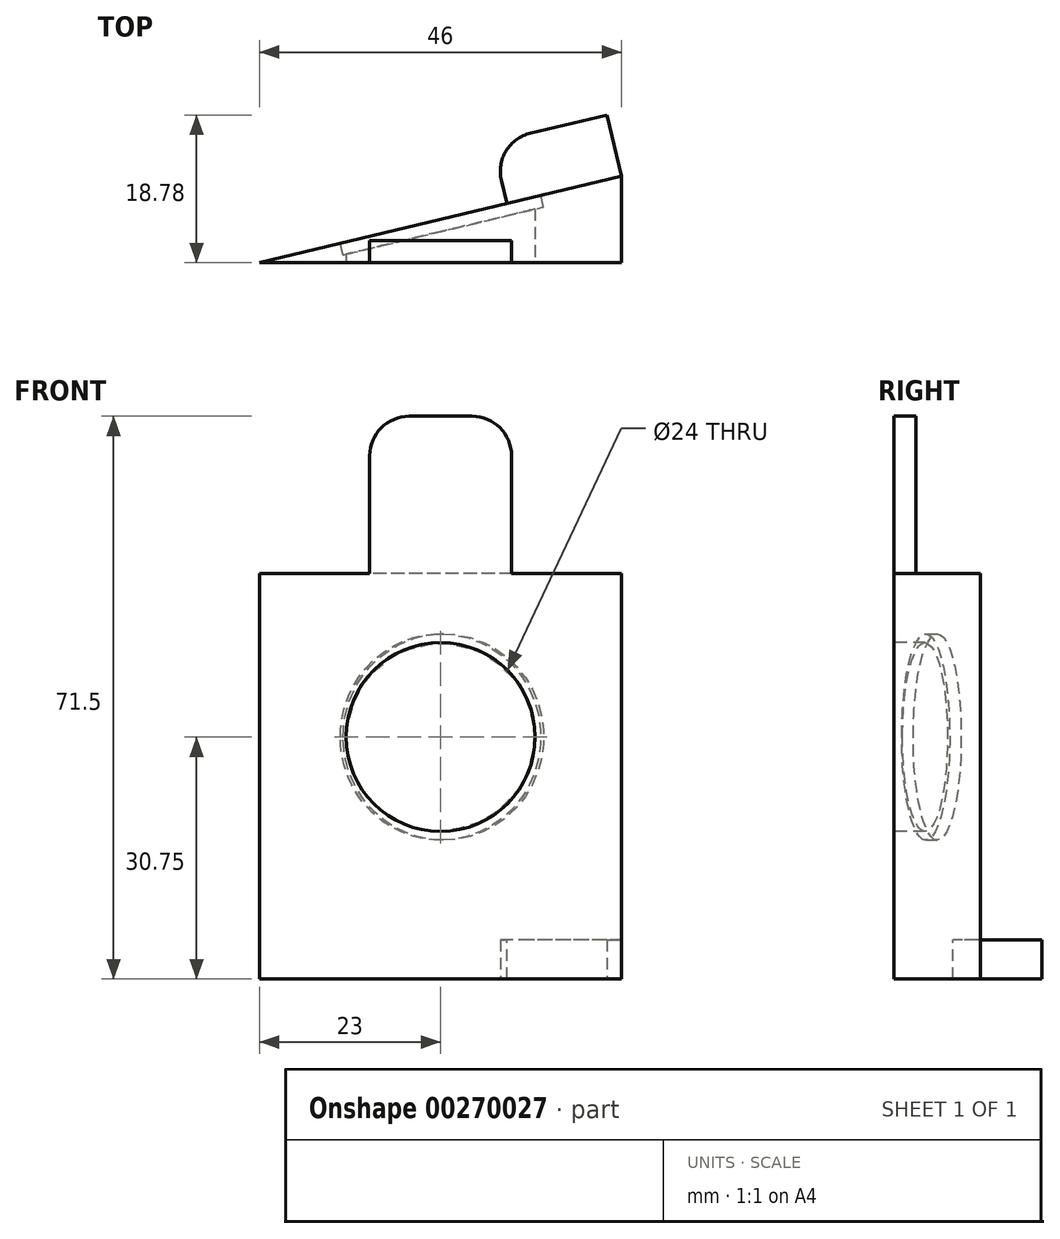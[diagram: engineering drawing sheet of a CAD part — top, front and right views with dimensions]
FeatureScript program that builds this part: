
annotation { "Feature Type Name" : "Feature", "Feature Type Description" : "" }
export const myFeature = defineFeature(function(context is Context, id is Id, definition is map)
    precondition{}
    {
        {
            var Q0;
            Q0=qCreatedBy(makeId("Top.planeOp"),FACE);
            var sketch = newSketch(context, id + "F0", { "sketchPlane" : qUnion([Q0])});
            skLineSegment(sketch, "E0", {"start": v(-23, 0) * mm, "end": v(23, 0) * mm});
            skLineSegment(sketch, "E1", {"start": v(23, 0) * mm, "end": v(23, 11) * mm});
            skLineSegment(sketch, "E2", {"start": v(23, 11) * mm, "end": v(-23, 0) * mm});
            skSolve(sketch);
        }
        {
            var Q0;
            Q0 = qSketchRegion(id + "F0", true);
            extrude(context, id + "F1", {"entities" : qUnion([Q0]), "depth" : 51.5 * mm});
        }
        {
            var Q0;
            Q0=makeQuery(id+"F1.opExtrude","SWEPT_FACE",FACE,{"disambiguationData":[OSD([sQuery(id+"F0.wireOp",EDGE,"E0")])]});
            var sketch = newSketch(context, id + "F2", { "sketchPlane" : qUnion([Q0])});
            skCircle(sketch, "E3", {"center": v(0, 30.75) * mm, "radius": 12 * mm});
            skSolve(sketch);
        }
        {
            var Q0;
            Q0 = qSketchRegion(id + "F2", true);
            extrude(context, id + "F3", {"entities" : qUnion([Q0]), "operationType" : NewBodyOperationType.REMOVE, "endBound" : BoundingType.THROUGH_ALL, "oppositeDirection" : true, "depth" : 25 * mm});
        }
        {
            var Q0;
            Q0=makeQuery(id+"F1.opExtrude","SWEPT_FACE",FACE,{"disambiguationData":[OSD([sQuery(id+"F0.wireOp",EDGE,"E2")])]});
            var sketch = newSketch(context, id + "F4", { "sketchPlane" : qUnion([Q0])});
            skCircle(sketch, "E4", {"center": v(-1.28, 30.75) * mm, "radius": 13.1 * mm});
            skSolve(sketch);
        }
        {
            var Q0;
            Q0 = qSketchRegion(id + "F4", true);
            extrude(context, id + "F5", {"entities" : qUnion([Q0]), "operationType" : NewBodyOperationType.REMOVE, "oppositeDirection" : true, "depth" : 1.5 * mm});
        }
        {
            var Q0;
            Q0=makeQuery(id+"F1.opExtrude","SWEPT_FACE",FACE,{"disambiguationData":[OSD([sQuery(id+"F0.wireOp",EDGE,"E2")])]});
            var sketch = newSketch(context, id + "F6", { "sketchPlane" : qUnion([Q0])});
            skLineSegment(sketch, "E5.bottom", {"start": v(-24.93, 0) * mm, "end": v(-9.93, 0) * mm});
            skLineSegment(sketch, "E5.top", {"start": v(-24.93, 5) * mm, "end": v(-9.93, 5) * mm});
            skLineSegment(sketch, "E5.left", {"start": v(-24.93, 0) * mm, "end": v(-24.93, 5) * mm});
            skLineSegment(sketch, "E5.right", {"start": v(-9.93, 0) * mm, "end": v(-9.93, 5) * mm});
            skSolve(sketch);
        }
        {
            var Q0;
            Q0 = qSketchRegion(id + "F6", true);
            extrude(context, id + "F7", {"entities" : qUnion([Q0]), "operationType" : NewBodyOperationType.ADD, "depth" : 8 * mm});
        }
        {
            var Q0;
            Q0=makeQuery(id+"F1.opExtrude","CAP_FACE",FACE,{"disambiguationData":[OSD([sQuery(id+"F0.wireOp",EDGE,"E0"),sQuery(id+"F0.wireOp",EDGE,"E1"),sQuery(id+"F0.wireOp",EDGE,"E2")])],"isStart":false});
            var sketch = newSketch(context, id + "F8", { "sketchPlane" : qUnion([Q0])});
            skLineSegment(sketch, "E6.bottom", {"start": v(9, 0) * mm, "end": v(-9, 0) * mm});
            skLineSegment(sketch, "E6.top", {"start": v(9, 2.8) * mm, "end": v(-9, 2.8) * mm});
            skLineSegment(sketch, "E6.left", {"start": v(9, 0) * mm, "end": v(9, 2.8) * mm});
            skLineSegment(sketch, "E6.right", {"start": v(-9, 0) * mm, "end": v(-9, 2.8) * mm});
            skSolve(sketch);
        }
        {
            var Q0;
            Q0 = qSketchRegion(id + "F8", true);
            extrude(context, id + "F9", {"entities" : qUnion([Q0]), "operationType" : NewBodyOperationType.ADD, "depth" : 20 * mm});
        }
        {
            var Q0;
            Q0=makeQuery(id+"F7.opExtrude","CAP_EDGE",EDGE,{"disambiguationData":[OSD([sQuery(id+"F6.wireOp",EDGE,"E5.right")])],"isStart":false});
            var Q1;
            Q1=makeQuery(id+"F9.opExtrude","CAP_EDGE",EDGE,{"disambiguationData":[OSD([sQuery(id+"F8.wireOp",EDGE,"E6.right")])],"isStart":false});
            var Q2;
            Q2=makeQuery(id+"F9.opExtrude","CAP_EDGE",EDGE,{"disambiguationData":[OSD([sQuery(id+"F8.wireOp",EDGE,"E6.left")])],"isStart":false});
            fillet(context, id + "F10", {"entities" : qUnion([Q0, Q1, Q2]), "radius" : 5 * mm, "tangentPropagation" : true, "allowEdgeOverflow" : false});
        }
    });
